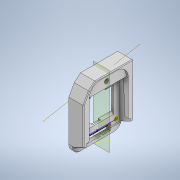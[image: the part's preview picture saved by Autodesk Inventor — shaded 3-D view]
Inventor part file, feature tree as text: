
AUTODESK INVENTOR PART (.ipt)
format: ipt  version: 2021.1 (Build 251245010, 245A)  size: 536,064 bytes
history: native  units: mm
features: sketch x22, extrude x17, other x14, chamfer x8, mirror x2, hole x1
ambient origin geometry x8: Origin, YZ Plane, XZ Plane, XY Plane, X Axis, Y Axis, Z Axis, Center Point
bodies: Body1 (feature_tree)
feature tree (64):
  other  "Поперечное сечение1"
  other  "Твердое тело1"
  extrude  "Выдавливание1"  Depth=21.0mm
  extrude  "Выдавливание2"  Depth=71.0mm
  extrude  "Выдавливание3"  Depth=92.0mm TaperAngle=0.0deg
  extrude  "Выдавливание4"  Depth=6.0mm
  extrude  "Выдавливание5"  Depth=4.6mm
  extrude  "Выдавливание6"  Depth=35.5mm
  sketch  "Эскиз7"
  extrude  "Выдавливание8"  Depth=71.0mm
  extrude  "Выдавливание9"  Depth=5.2mm
  extrude  "Выдавливание10"  Depth=7.7mm
  extrude  "Выдавливание11"  Depth=49.0mm TaperAngle=0.0deg
  extrude  "Выдавливание12"  Depth=55.6mm
  mirror  "Зеркальное отражение2"
  hole  "Отверстие1"  [1 undecoded]
  extrude  "Выдавливание13"  Depth=8.8mm
  sketch  "Эскиз17"
  sketch  "Эскиз18"
  other  "РабПлоскость1"
  extrude  "Выдавливание14"  Depth=2.5mm
  extrude  "Выдавливание15"  Depth=3.1mm TaperAngle=0.0deg
  chamfer  "Фаска1"  Distance=71.0mm
  chamfer  "Фаска2"  Distance=2.0mm
  extrude  "Выдавливание17"  Depth=3.0mm TaperAngle=0.0deg
  extrude  "Выдавливание18"  TaperAngle=45.0deg  [1 undecoded]
  sketch  "Эскиз26"
  sketch  "Эскиз27"
  other  "РабПлоскость3"
  extrude  "Выдавливание19"  Depth=25.0mm
  chamfer  "Фаска4"  Distance=10.0mm
  chamfer  "Фаска5"  Distance=3.0mm
  chamfer  "Фаска6"  Distance=10.0mm
  chamfer  "Фаска7"  Distance=16.0mm
  chamfer  "Фаска8"  Distance=6.0mm
  other  "РабПлоскость4"
  mirror  "Зеркальное отражение3"
  chamfer  "Фаска9"  Distance=6.0mm
  sketch  "Эскиз1"
  sketch  "Эскиз2"
  sketch  "Эскиз3"
  sketch  "Эскиз4"
  sketch  "Эскиз5"
  sketch  "Эскиз6"
  sketch  "Эскиз8"
  sketch  "Эскиз9"
  sketch  "Эскиз10"
  sketch  "Эскиз11"
  sketch  "Эскиз13"
  sketch  "Эскиз15"
  sketch  "Эскиз16"
  sketch  "Эскиз19"
  sketch  "Эскиз20"
  sketch  "Эскиз24"
  other  "РабОсь1"
  sketch  "Эскиз28"
  other  "Проецирование ребер1"
  other  "Проецирование ребер2"
  other  "Проецирование ребер3"
  other  "Проецирование ребер4"
  other  "Проецирование ребер5"
  other  "Проецирование ребер6"
  other  "Проецирование ребер7"
  other  "Проецирование ребер8"
note: 2 required parameter values undecoded (feature->parameter linkage not recoverable at this tier; creation-order binding heuristic only, values carry confidence <= 0.55)
